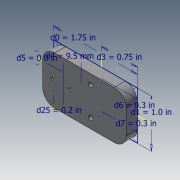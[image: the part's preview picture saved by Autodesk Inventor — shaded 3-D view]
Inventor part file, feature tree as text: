
AUTODESK INVENTOR PART (.ipt)
format: ipt  version: 2018.3 (Build 223284000, 284)  size: 120,320 bytes
history: native  units: in
note: dims shown in document units (in); Inventor stores cm internally (conversion verified against a paired STEP export)
features: hole x2, sketch x1, extrude x1, fillet x1
ambient origin geometry x8: Origin, YZ Plane, XZ Plane, XY Plane, X Axis, Y Axis, Z Axis, Center Point
bodies: Solid1 (feature_tree)
feature tree (5):
  sketch  "Sketch1"  dims[d0=1.75in d1=1.0in d3=0.75in d4=0.374in d5=0.0in d6=0.3in d7=0.3in d8=0.23in d9=0.0in d10=0.059in d11=0.75in d12=0.375in d13=0.25in d14=0.5635in d15=1.0in d16=0.8108in d17=0.093in d18=0.75in d19=0.375in d20=0.25in d21=0.5635in d22=1.0in d23=0.8108in d24=0.25in d25=0.2in]
  extrude  "Extrusion1"  Depth=1.0in
  hole  "Hole1"  [1 undecoded]
  hole  "Hole2"  [1 undecoded]
  fillet  "Fillet1"  [1 undecoded]
note: 3 required parameter values undecoded (feature->parameter linkage not recoverable at this tier; creation-order binding heuristic only, values carry confidence <= 0.55)
